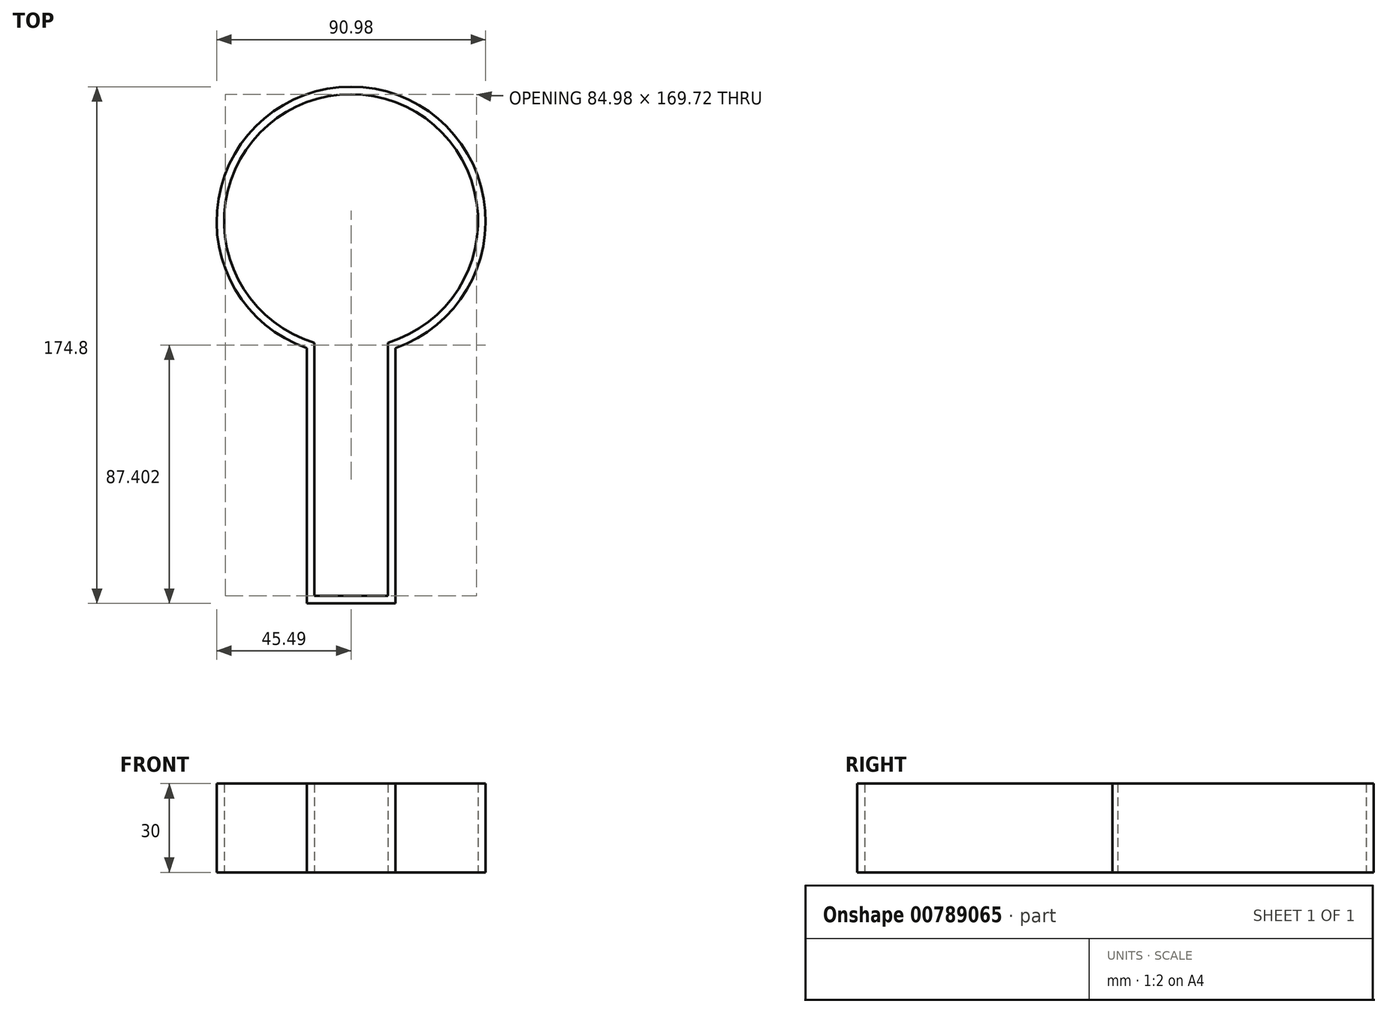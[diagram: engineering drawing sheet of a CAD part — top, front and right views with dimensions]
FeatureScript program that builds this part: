
annotation { "Feature Type Name" : "Feature", "Feature Type Description" : "" }
export const myFeature = defineFeature(function(context is Context, id is Id, definition is map)
    precondition{}
    {
        {
            var Q0;
            Q0=qCreatedBy(makeId("Top.planeOp"),FACE);
            var sketch = newSketch(context, id + "F0", { "sketchPlane" : qUnion([Q0])});
            skArc(sketch, "E0", {"start": v(15, -42.95) * mm, "mid": v(0, 45.5) * mm, "end": v(-15, -42.95) * mm});
            skLineSegment(sketch, "E1.bottom", {"start": v(-21, -130.81) * mm, "end": v(0, -130.81) * mm});
            skLineSegment(sketch, "E1.top", {"start": v(-21, -194.31) * mm, "end": v(0, -194.31) * mm});
            skLineSegment(sketch, "E1.left", {"start": v(-21, -130.81) * mm, "end": v(-21, -194.31) * mm});
            skLineSegment(sketch, "E1.right", {"start": v(0, -130.81) * mm, "end": v(0, -194.31) * mm});
            skLineSegment(sketch, "E2.top", {"start": v(-15, -129.3) * mm, "end": v(15, -129.3) * mm});
            skLineSegment(sketch, "E2.left", {"start": v(-15, -42.95) * mm, "end": v(-15, -129.3) * mm});
            skLineSegment(sketch, "E2.right", {"start": v(15, -42.95) * mm, "end": v(15, -129.3) * mm});
            skSolve(sketch);
        }
        {
            var Q0;
            Q0=makeQuery(id+"F0.imprint","IMPRINT",FACE,{"disambiguationData":[TD([[makeQuery(id+"F0.imprint","IMPRINT",EDGE,{"derivedFrom":sQuery(id+"F0.wireOp",EDGE,"E2.top")}),1.0]])]});
            extrude(context, id + "F1", {"entities" : qUnion([Q0]), "depth" : 30 * mm, "offsetDistance" : 25.4 * mm});
        }
        {
            var Q0;
            Q0=makeQuery(id+"F1.opExtrude","CAP_FACE",FACE,{"disambiguationData":[OSD([sQuery(id+"F0.wireOp",EDGE,"E0"),sQuery(id+"F0.wireOp",EDGE,"E2.bottom"),sQuery(id+"F0.wireOp",EDGE,"E2.top"),sQuery(id+"F0.wireOp",EDGE,"E2.left"),sQuery(id+"F0.wireOp",EDGE,"E2.right")])],"isStart":false});
            var Q1;
            Q1=makeQuery(id+"F1.opExtrude","CAP_FACE",FACE,{"disambiguationData":[OSD([sQuery(id+"F0.wireOp",EDGE,"E0"),sQuery(id+"F0.wireOp",EDGE,"E2.bottom"),sQuery(id+"F0.wireOp",EDGE,"E2.top"),sQuery(id+"F0.wireOp",EDGE,"E2.left"),sQuery(id+"F0.wireOp",EDGE,"E2.right")])],"isStart":true});
            shell(context, id + "F2", {"entities" : qUnion([Q0, Q1]), "thickness" : 2.54 * mm});
        }
    });
